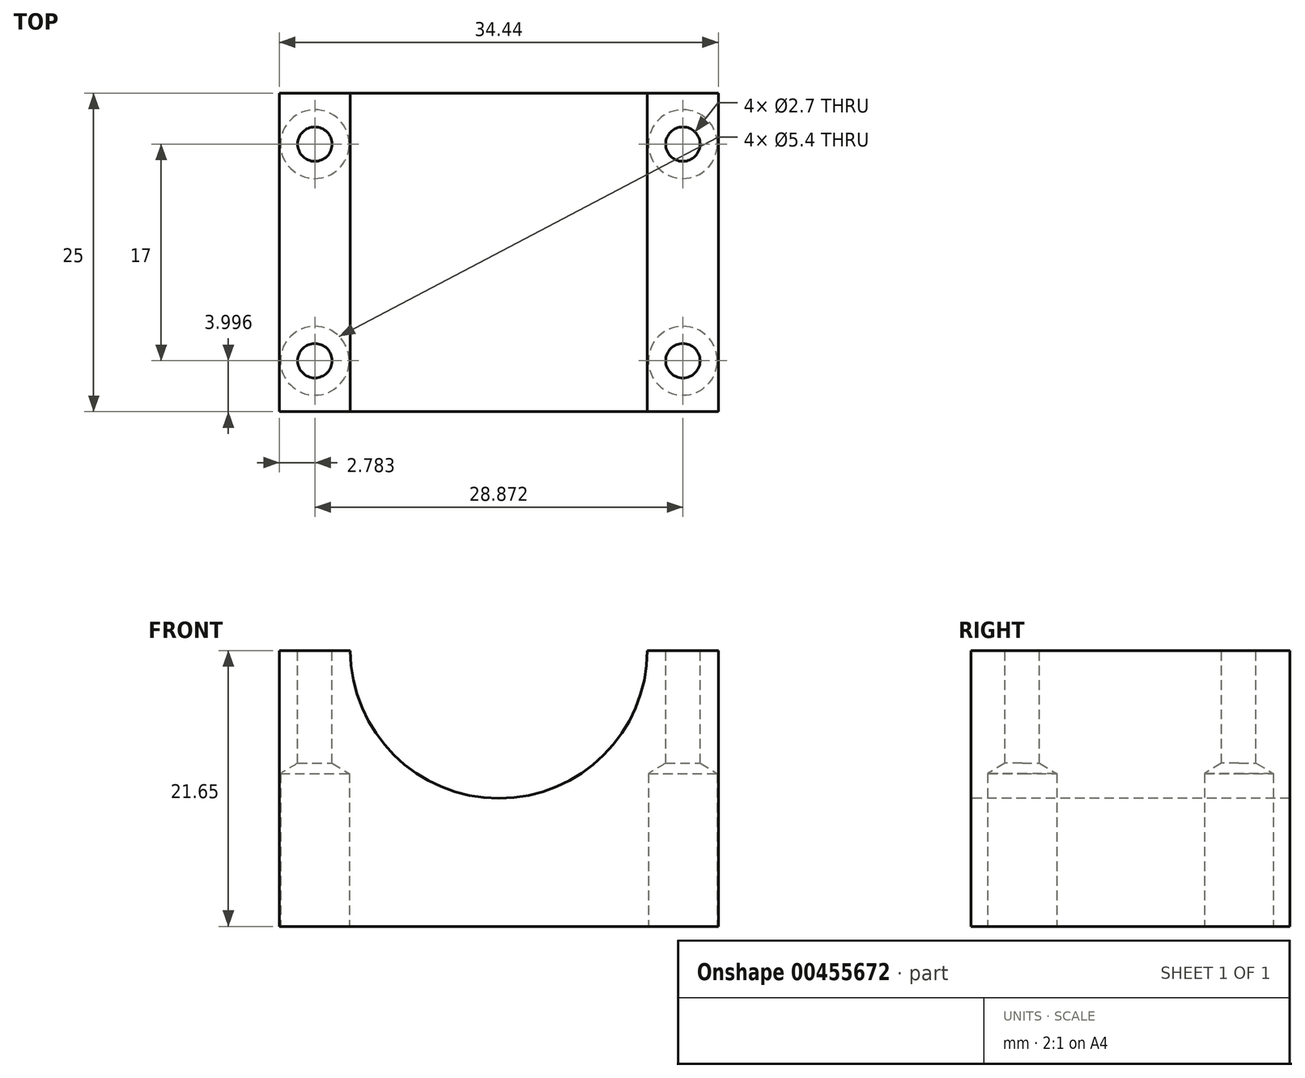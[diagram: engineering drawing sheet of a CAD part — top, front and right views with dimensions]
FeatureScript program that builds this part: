
annotation { "Feature Type Name" : "Feature", "Feature Type Description" : "" }
export const myFeature = defineFeature(function(context is Context, id is Id, definition is map)
    precondition{}
    {
        {
            var Q0;
            Q0=qCreatedBy(makeId("Top.planeOp"),FACE);
            var sketch = newSketch(context, id + "F0", { "sketchPlane" : qUnion([Q0])});
            skLineSegment(sketch, "E0.bottom", {"start": v(-58.93, 30.62) * mm, "end": v(-24.49, 30.62) * mm});
            skLineSegment(sketch, "E0.top", {"start": v(-58.93, 5.62) * mm, "end": v(-24.49, 5.62) * mm});
            skLineSegment(sketch, "E0.left", {"start": v(-58.93, 30.62) * mm, "end": v(-58.93, 5.62) * mm});
            skLineSegment(sketch, "E0.right", {"start": v(-24.49, 30.62) * mm, "end": v(-24.49, 5.62) * mm});
            skSolve(sketch);
        }
        {
            var Q0;
            Q0=makeQuery(id+"F0.imprint","IMPRINT",FACE,{"disambiguationData":[TD([[makeQuery(id+"F0.imprint","IMPRINT",EDGE,{"derivedFrom":sQuery(id+"F0.wireOp",EDGE,"E0.bottom")}),-1.0]])]});
            extrude(context, id + "F1", {"entities" : qUnion([Q0]), "depth" : (10 + (23.3 / 2)) * mm});
        }
        {
            var Q0;
            Q0=makeQuery(id+"F1.opExtrude","SWEPT_FACE",FACE,{"disambiguationData":[OSD([sQuery(id+"F0.wireOp",EDGE,"E0.top")])]});
            var sketch = newSketch(context, id + "F2", { "sketchPlane" : qUnion([Q0])});
            skCircle(sketch, "E1", {"center": v(-41.71, 21.7) * mm, "radius": 11.7 * mm});
            skSolve(sketch);
        }
        {
            var Q0;
            Q0=sQuery(id+"F2.wireOp",VERTEX,"E1.center");
            var Q1;
            Q1=makeQuery(id+"F1.opExtrude","SWEPT_BODY",BODY,{"disambiguationData":[OSD([sQuery(id+"F0.wireOp",EDGE,"E0.bottom"),sQuery(id+"F0.wireOp",EDGE,"E0.top"),sQuery(id+"F0.wireOp",EDGE,"E0.left"),sQuery(id+"F0.wireOp",EDGE,"E0.right")])]});
            hole(context, id + "F3", {"style" : HoleStyle.SIMPLE, "endStyle" : HoleEndStyle.THROUGH, "holeDiameter" : 23.3 * mm, "isTappedThrough" : true, "tappedDepth" : 12 * mm, "tapClearance" : 3, "locations" : qUnion([Q0]), "scope" : qUnion([Q1])});
        }
        {
            var Q0;
            {var subQ0=sQuery(id+"F0.wireOp",EDGE,"E0.bottom");var subQ1=sQuery(id+"F0.wireOp",EDGE,"E0.top");var subQ2=sQuery(id+"F0.wireOp",EDGE,"E0.left");Q0=makeQuery(id+"F3.hole-0.boolean.opBoolean","SPLIT",FACE,{"disambiguationData":[TD([makeQuery(id+"F1.opExtrude","SWEPT_FACE",FACE,{"disambiguationData":[OSD([subQ2])]})])],"derivedFrom":makeQuery(id+"F1.opExtrude","CAP_FACE",FACE,{"disambiguationData":[OSD([subQ0,subQ1,subQ2,sQuery(id+"F0.wireOp",EDGE,"E0.right")])],"isStart":false})});}
            var sketch = newSketch(context, id + "F4", { "sketchPlane" : qUnion([Q0])});
            skCircle(sketch, "E2", {"center": v(-56.15, 26.62) * mm, "radius": 1.4 * mm});
            skCircle(sketch, "E3", {"center": v(-56.15, 9.62) * mm, "radius": 1.4 * mm});
            skCircle(sketch, "E4", {"center": v(-27.27, 9.62) * mm, "radius": 1.4 * mm});
            skCircle(sketch, "E5", {"center": v(-27.27, 26.62) * mm, "radius": 1.4 * mm});
            skSolve(sketch);
        }
        {
            var Q0;
            Q0=sQuery(id+"F4.wireOp",VERTEX,"E2.center");
            var Q1;
            Q1=sQuery(id+"F4.wireOp",VERTEX,"E3.center");
            var Q2;
            Q2=sQuery(id+"F4.wireOp",VERTEX,"E4.center");
            var Q3;
            Q3=sQuery(id+"F4.wireOp",VERTEX,"E5.center");
            var Q4;
            Q4=makeQuery(id+"F1.opExtrude","SWEPT_BODY",BODY,{"disambiguationData":[OSD([sQuery(id+"F0.wireOp",EDGE,"E0.bottom"),sQuery(id+"F0.wireOp",EDGE,"E0.top"),sQuery(id+"F0.wireOp",EDGE,"E0.left"),sQuery(id+"F0.wireOp",EDGE,"E0.right")])]});
            hole(context, id + "F5", {"style" : HoleStyle.SIMPLE, "endStyle" : HoleEndStyle.THROUGH, "holeDiameter" : 2.7 * mm, "isTappedThrough" : true, "tappedDepth" : 12 * mm, "tapClearance" : 3, "locations" : qUnion([Q0, Q1, Q2, Q3]), "scope" : qUnion([Q4])});
        }
        {
            var Q0;
            Q0=makeQuery(id+"F1.opExtrude","CAP_FACE",FACE,{"disambiguationData":[OSD([sQuery(id+"F0.wireOp",EDGE,"E0.bottom"),sQuery(id+"F0.wireOp",EDGE,"E0.top"),sQuery(id+"F0.wireOp",EDGE,"E0.left"),sQuery(id+"F0.wireOp",EDGE,"E0.right")])],"isStart":true});
            var sketch = newSketch(context, id + "F6", { "sketchPlane" : qUnion([Q0])});
            skPoint(sketch, "E6", {"position": v(-56.15, -9.62) * mm});
            skPoint(sketch, "E7", {"position": v(-56.15, -26.62) * mm});
            skPoint(sketch, "E8", {"position": v(-27.27, -26.62) * mm});
            skPoint(sketch, "E9", {"position": v(-27.27, -9.62) * mm});
            skSolve(sketch);
        }
        {
            var Q0;
            Q0=sQuery(id+"F6.wireOp",VERTEX,"E6");
            var Q1;
            Q1=sQuery(id+"F6.wireOp",VERTEX,"E7");
            var Q2;
            Q2=sQuery(id+"F6.wireOp",VERTEX,"E8");
            var Q3;
            Q3=sQuery(id+"F6.wireOp",VERTEX,"E9");
            var Q4;
            Q4=makeQuery(id+"F1.opExtrude","SWEPT_BODY",BODY,{"disambiguationData":[OSD([sQuery(id+"F0.wireOp",EDGE,"E0.bottom"),sQuery(id+"F0.wireOp",EDGE,"E0.top"),sQuery(id+"F0.wireOp",EDGE,"E0.left"),sQuery(id+"F0.wireOp",EDGE,"E0.right")])]});
            hole(context, id + "F7", {"style" : HoleStyle.SIMPLE, "endStyle" : HoleEndStyle.BLIND, "holeDiameter" : 5.4 * mm, "holeDepth" : 12 * mm, "isTappedThrough" : true, "tappedDepth" : 12 * mm, "tapClearance" : 3, "locations" : qUnion([Q0, Q1, Q2, Q3]), "scope" : qUnion([Q4])});
        }
    });
